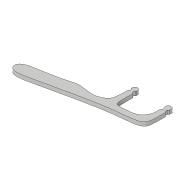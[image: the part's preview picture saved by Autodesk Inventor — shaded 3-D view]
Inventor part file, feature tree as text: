
AUTODESK INVENTOR PART (.ipt)
format: ipt  version: 2019.4 (Build 234330000, 330)  size: 276,992 bytes
history: native  units: mm
features: extrude x2, fillet x2, sketch x2, other x1, projected_geometry x1
ambient origin geometry x8: Origin, YZ Plane, XZ Plane, XY Plane, X Axis, Y Axis, Z Axis, Center Point
bodies: Solid1 (feature_tree)
feature tree (8):
  extrude  "Extrusion1"  Depth=5.0mm
  fillet  "Fillet1"  Radius=1.5mm
  extrude  "Extrusion2"  [1 undecoded]
  fillet  "Fillet2"  [1 undecoded]
  sketch  "Sketch1"  dims[d3=1.5mm d4=0.0mm d5=5.0mm d6=1.5mm d7=0.0mm]
  other  "Image1"
  sketch  "Sketch2"  dims[d8=0.5mm]
  projected_geometry  "Projected Loop1"
note: 2 required parameter values undecoded (feature->parameter linkage not recoverable at this tier; creation-order binding heuristic only, values carry confidence <= 0.55)
